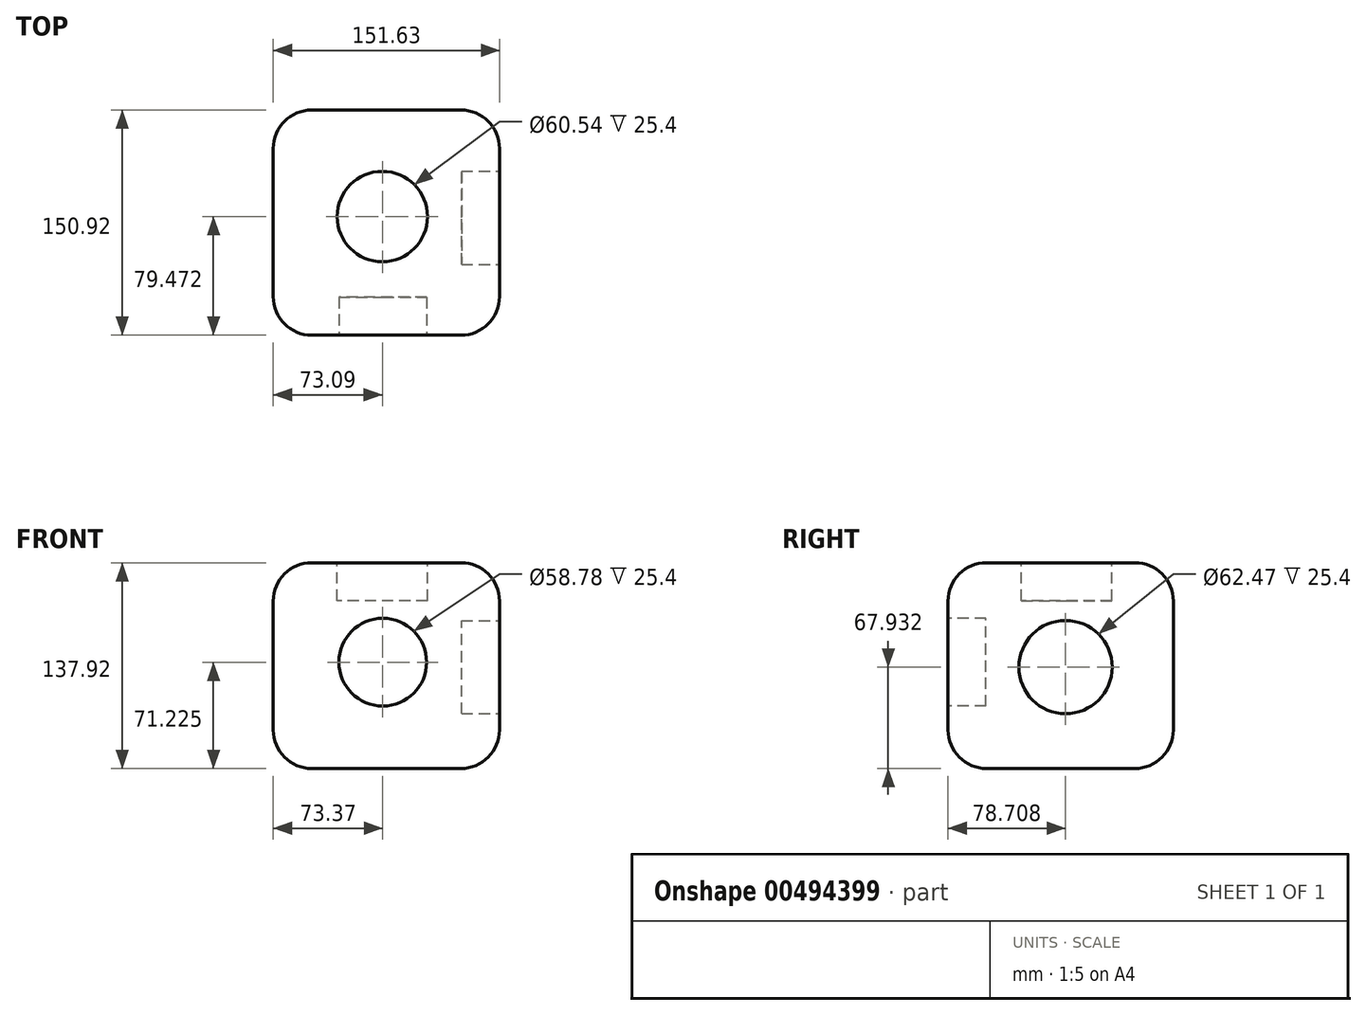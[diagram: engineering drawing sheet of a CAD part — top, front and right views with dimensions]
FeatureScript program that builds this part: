
annotation { "Feature Type Name" : "Feature", "Feature Type Description" : "" }
export const myFeature = defineFeature(function(context is Context, id is Id, definition is map)
    precondition{}
    {
        {
            var Q0;
            Q0=qCreatedBy(makeId("Top.planeOp"),FACE);
            var sketch = newSketch(context, id + "F0", { "sketchPlane" : qUnion([Q0])});
            skLineSegment(sketch, "E0.bottom", {"start": v(-75.3, 74.89) * mm, "end": v(76.33, 74.89) * mm});
            skLineSegment(sketch, "E0.top", {"start": v(-75.3, -76.03) * mm, "end": v(76.33, -76.03) * mm});
            skLineSegment(sketch, "E0.left", {"start": v(-75.3, 74.89) * mm, "end": v(-75.3, -76.03) * mm});
            skLineSegment(sketch, "E0.right", {"start": v(76.33, 74.89) * mm, "end": v(76.33, -76.03) * mm});
            skSolve(sketch);
        }
        {
            var Q0;
            Q0=makeQuery(id+"F0.imprint","IMPRINT",FACE,{"disambiguationData":[TD([[makeQuery(id+"F0.imprint","IMPRINT",EDGE,{"derivedFrom":sQuery(id+"F0.wireOp",EDGE,"E0.bottom")}),-1.0]])]});
            extrude(context, id + "F1", {"entities" : qUnion([Q0]), "depth" : 137.92 * mm});
        }
        {
            var Q0;
            Q0=makeQuery(id+"F1.opExtrude","CAP_FACE",FACE,{"disambiguationData":[OSD([sQuery(id+"F0.wireOp",EDGE,"E0.bottom"),sQuery(id+"F0.wireOp",EDGE,"E0.top"),sQuery(id+"F0.wireOp",EDGE,"E0.left"),sQuery(id+"F0.wireOp",EDGE,"E0.right")])],"isStart":false});
            var Q1;
            Q1=makeQuery(id+"F1.opExtrude","SWEPT_FACE",FACE,{"disambiguationData":[OSD([sQuery(id+"F0.wireOp",EDGE,"E0.right")])]});
            var Q2;
            Q2=makeQuery(id+"F1.opExtrude","SWEPT_FACE",FACE,{"disambiguationData":[OSD([sQuery(id+"F0.wireOp",EDGE,"E0.top")])]});
            var Q3;
            Q3=makeQuery(id+"F1.opExtrude","SWEPT_FACE",FACE,{"disambiguationData":[OSD([sQuery(id+"F0.wireOp",EDGE,"E0.left")])]});
            var Q4;
            Q4=makeQuery(id+"F1.opExtrude","SWEPT_FACE",FACE,{"disambiguationData":[OSD([sQuery(id+"F0.wireOp",EDGE,"E0.bottom")])]});
            var Q5;
            Q5=makeQuery(id+"F1.opExtrude","CAP_FACE",FACE,{"disambiguationData":[OSD([sQuery(id+"F0.wireOp",EDGE,"E0.bottom"),sQuery(id+"F0.wireOp",EDGE,"E0.top"),sQuery(id+"F0.wireOp",EDGE,"E0.left"),sQuery(id+"F0.wireOp",EDGE,"E0.right")])],"isStart":true});
            fillet(context, id + "F2", {"entities" : qUnion([Q0, Q1, Q2, Q3, Q4, Q5]), "radius" : 25.75 * mm, "tangentPropagation" : true, "allowEdgeOverflow" : false});
        }
        {
            var Q0;
            Q0=makeQuery(id+"F1.opExtrude","CAP_FACE",FACE,{"disambiguationData":[OSD([sQuery(id+"F0.wireOp",EDGE,"E0.bottom"),sQuery(id+"F0.wireOp",EDGE,"E0.top"),sQuery(id+"F0.wireOp",EDGE,"E0.left"),sQuery(id+"F0.wireOp",EDGE,"E0.right")])],"isStart":false});
            var sketch = newSketch(context, id + "F3", { "sketchPlane" : qUnion([Q0])});
            skCircle(sketch, "E1", {"center": v(-2.21, 3.44) * mm, "radius": 30.27 * mm});
            skSolve(sketch);
        }
        {
            var Q0;
            Q0 = qSketchRegion(id + "F3", true);
            extrude(context, id + "F4", {"entities" : qUnion([Q0]), "operationType" : NewBodyOperationType.REMOVE, "oppositeDirection" : true, "depth" : 25.4 * mm});
        }
        {
            var Q0;
            Q0=makeQuery(id+"F1.opExtrude","SWEPT_FACE",FACE,{"disambiguationData":[OSD([sQuery(id+"F0.wireOp",EDGE,"E0.top")])]});
            var sketch = newSketch(context, id + "F5", { "sketchPlane" : qUnion([Q0])});
            skCircle(sketch, "E2", {"center": v(-1.93, 71.22) * mm, "radius": 29.39 * mm});
            skSolve(sketch);
        }
        {
            var Q0;
            Q0=makeQuery(id+"F5.imprint","IMPRINT",FACE,{"disambiguationData":[TD([[makeQuery(id+"F5.imprint","IMPRINT",EDGE,{"derivedFrom":sQuery(id+"F5.wireOp",EDGE,"E2")}),1.0]])]});
            extrude(context, id + "F6", {"entities" : qUnion([Q0]), "operationType" : NewBodyOperationType.REMOVE, "oppositeDirection" : true, "depth" : 25.4 * mm});
        }
        {
            var Q0;
            Q0=makeQuery(id+"F1.opExtrude","SWEPT_FACE",FACE,{"disambiguationData":[OSD([sQuery(id+"F0.wireOp",EDGE,"E0.right")])]});
            var sketch = newSketch(context, id + "F7", { "sketchPlane" : qUnion([Q0])});
            skCircle(sketch, "E3", {"center": v(2.68, 67.93) * mm, "radius": 31.23 * mm});
            skSolve(sketch);
        }
        {
            var Q0;
            Q0 = qSketchRegion(id + "F7", true);
            extrude(context, id + "F8", {"entities" : qUnion([Q0]), "operationType" : NewBodyOperationType.REMOVE, "oppositeDirection" : true, "depth" : 25.4 * mm});
        }
    });
